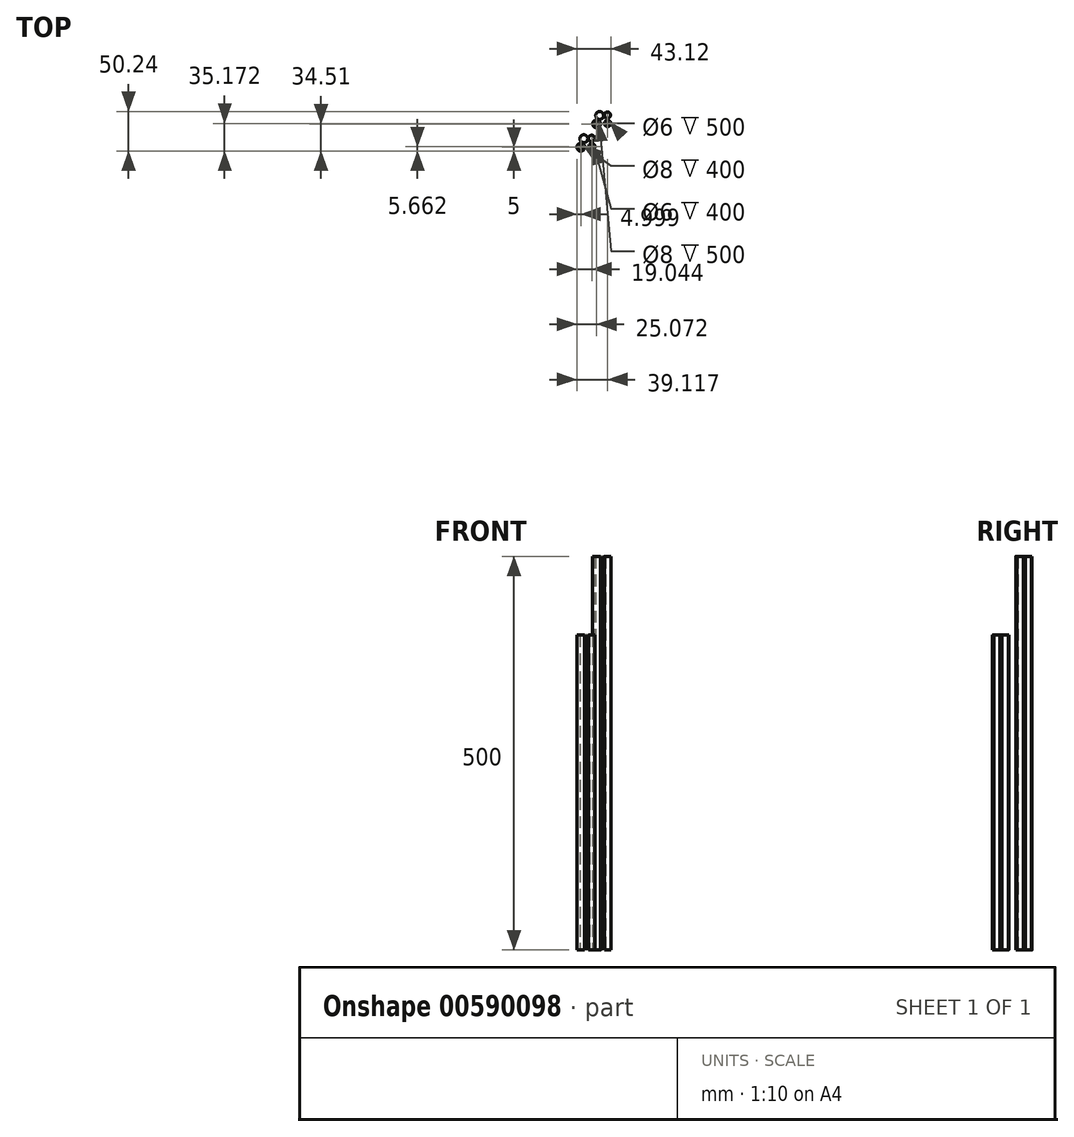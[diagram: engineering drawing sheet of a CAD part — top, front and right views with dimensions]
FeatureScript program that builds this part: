
annotation { "Feature Type Name" : "Feature", "Feature Type Description" : "" }
export const myFeature = defineFeature(function(context is Context, id is Id, definition is map)
    precondition{}
    {
        {
            var Q0;
            Q0=qCreatedBy(makeId("Top.planeOp"),FACE);
            var sketch = newSketch(context, id + "F0", { "sketchPlane" : qUnion([Q0])});
            skCircle(sketch, "E0", {"center": v(-54.58, 54.93) * mm, "radius": 5 * mm});
            skCircle(sketch, "E1", {"center": v(-44.64, 55.33) * mm, "radius": 4 * mm});
            skCircle(sketch, "E2", {"center": v(-58.42, 44.2) * mm, "radius": 4 * mm});
            skCircle(sketch, "E3", {"center": v(-58.42, 44.2) * mm, "radius": 5 * mm});
            skCircle(sketch, "E4", {"center": v(-44.37, 44.86) * mm, "radius": 3 * mm});
            skCircle(sketch, "E5", {"center": v(-44.37, 44.86) * mm, "radius": 4 * mm});
            skSolve(sketch);
        }
        {
            var Q0;
            Q0 = qSketchRegion(id + "F0", true);
            extrude(context, id + "F1", {"entities" : qUnion([Q0]), "depth" : 500 * mm, "offsetDistance" : 25 * mm});
        }
        {
            var Q0;
            Q0=qCreatedBy(makeId("Top.planeOp"),FACE);
            var sketch = newSketch(context, id + "F2", { "sketchPlane" : qUnion([Q0])});
            skCircle(sketch, "E6", {"center": v(-74.65, 25.42) * mm, "radius": 5 * mm});
            skCircle(sketch, "E7", {"center": v(-64.71, 25.82) * mm, "radius": 4 * mm});
            skCircle(sketch, "E8", {"center": v(-78.5, 14.69) * mm, "radius": 4 * mm});
            skCircle(sketch, "E9", {"center": v(-78.5, 14.69) * mm, "radius": 5 * mm});
            skCircle(sketch, "E10", {"center": v(-64.45, 15.35) * mm, "radius": 3 * mm});
            skCircle(sketch, "E11", {"center": v(-64.45, 15.35) * mm, "radius": 4 * mm});
            skSolve(sketch);
        }
        {
            var Q0;
            Q0 = qSketchRegion(id + "F2", true);
            extrude(context, id + "F3", {"entities" : qUnion([Q0]), "depth" : 400 * mm, "offsetDistance" : 25 * mm});
        }
    });
